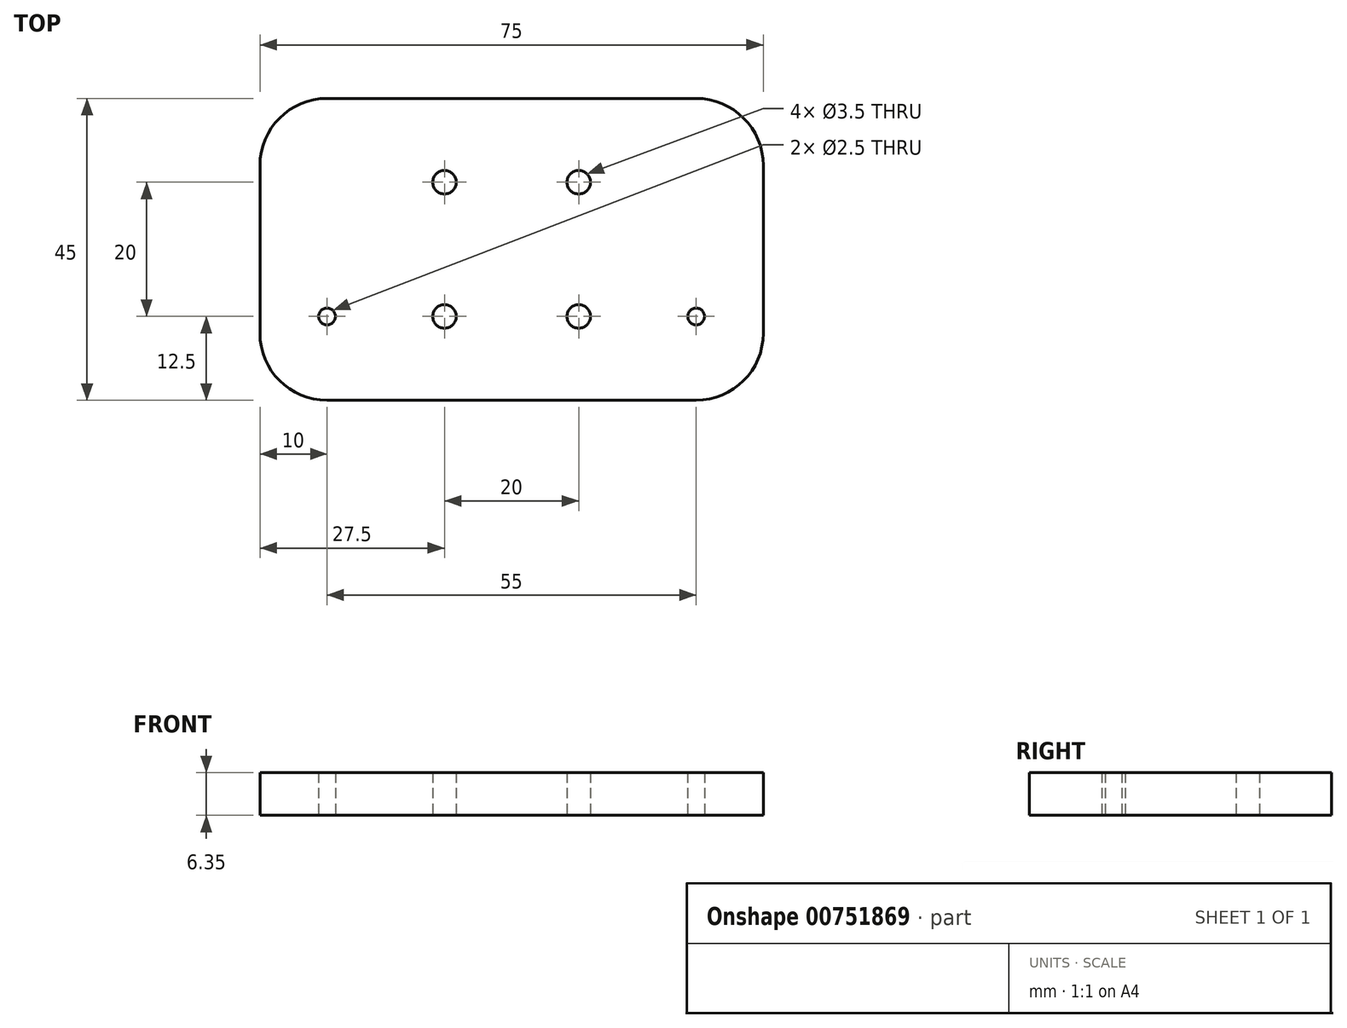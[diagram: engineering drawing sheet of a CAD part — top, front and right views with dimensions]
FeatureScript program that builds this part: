
annotation { "Feature Type Name" : "Feature", "Feature Type Description" : "" }
export const myFeature = defineFeature(function(context is Context, id is Id, definition is map)
    precondition{}
    {
        {
            var Q0;
            Q0=qCreatedBy(makeId("Top.planeOp"),FACE);
            var sketch = newSketch(context, id + "F0", { "sketchPlane" : qUnion([Q0])});
            skLineSegment(sketch, "E0.bottom", {"start": v(37.5, -22.5) * mm, "end": v(-37.5, -22.5) * mm});
            skLineSegment(sketch, "E0.top", {"start": v(37.5, 22.5) * mm, "end": v(-37.5, 22.5) * mm});
            skLineSegment(sketch, "E0.left", {"start": v(37.5, -22.5) * mm, "end": v(37.5, 22.5) * mm});
            skLineSegment(sketch, "E0.right", {"start": v(-37.5, -22.5) * mm, "end": v(-37.5, 22.5) * mm});
            skPoint(sketch, "E0.middle", {"position": v(0, 0) * mm});
            skLineSegment(sketch, "E1.bottom", {"start": v(10, -10) * mm, "end": v(-10, -10) * mm, "construction": true});
            skLineSegment(sketch, "E1.top", {"start": v(10, 10) * mm, "end": v(-10, 10) * mm, "construction": true});
            skLineSegment(sketch, "E1.left", {"start": v(10, -10) * mm, "end": v(10, 10) * mm, "construction": true});
            skLineSegment(sketch, "E1.right", {"start": v(-10, -10) * mm, "end": v(-10, 10) * mm, "construction": true});
            skCircle(sketch, "E2", {"center": v(-10, 10) * mm, "radius": 1.75 * mm});
            skCircle(sketch, "E3", {"center": v(10, 10) * mm, "radius": 1.75 * mm});
            skCircle(sketch, "E4", {"center": v(10, -10) * mm, "radius": 1.75 * mm});
            skCircle(sketch, "E5", {"center": v(-10, -10) * mm, "radius": 1.75 * mm});
            skLineSegment(sketch, "E6", {"start": v(-27.5, -10) * mm, "end": v(27.5, -10) * mm, "construction": true});
            skPoint(sketch, "E7", {"position": v(0, -10) * mm});
            skCircle(sketch, "E8", {"center": v(-27.5, -10) * mm, "radius": 1.25 * mm});
            skCircle(sketch, "E9", {"center": v(27.5, -10) * mm, "radius": 1.25 * mm});
            skSolve(sketch);
        }
        {
            var Q0;
            Q0=makeQuery(id+"F0.imprint","IMPRINT",FACE,{"disambiguationData":[TD([[makeQuery(id+"F0.imprint","IMPRINT",EDGE,{"derivedFrom":sQuery(id+"F0.wireOp",EDGE,"E0.bottom")}),-1.0]])]});
            extrude(context, id + "F1", {"entities" : qUnion([Q0]), "depth" : (.25 * 25.4) * mm, "offsetDistance" : 25 * mm});
        }
        {
            var Q0;
            Q0=makeQuery(id+"F1.opExtrude","SWEPT_EDGE",EDGE,{"disambiguationData":[OSD([sQuery(id+"F0.wireOp",EDGE,"E0.top"),sQuery(id+"F0.wireOp",EDGE,"E0.right")])]});
            var Q1;
            Q1=makeQuery(id+"F1.opExtrude","SWEPT_EDGE",EDGE,{"disambiguationData":[OSD([sQuery(id+"F0.wireOp",EDGE,"E0.top"),sQuery(id+"F0.wireOp",EDGE,"E0.left")])]});
            var Q2;
            Q2=makeQuery(id+"F1.opExtrude","SWEPT_EDGE",EDGE,{"disambiguationData":[OSD([sQuery(id+"F0.wireOp",EDGE,"E0.bottom"),sQuery(id+"F0.wireOp",EDGE,"E0.left")])]});
            var Q3;
            Q3=makeQuery(id+"F1.opExtrude","SWEPT_EDGE",EDGE,{"disambiguationData":[OSD([sQuery(id+"F0.wireOp",EDGE,"E0.bottom"),sQuery(id+"F0.wireOp",EDGE,"E0.right")])]});
            fillet(context, id + "F2", {"entities" : qUnion([Q0, Q1, Q2, Q3]), "radius" : 10 * mm, "tangentPropagation" : true, "allowEdgeOverflow" : false});
        }
    });
